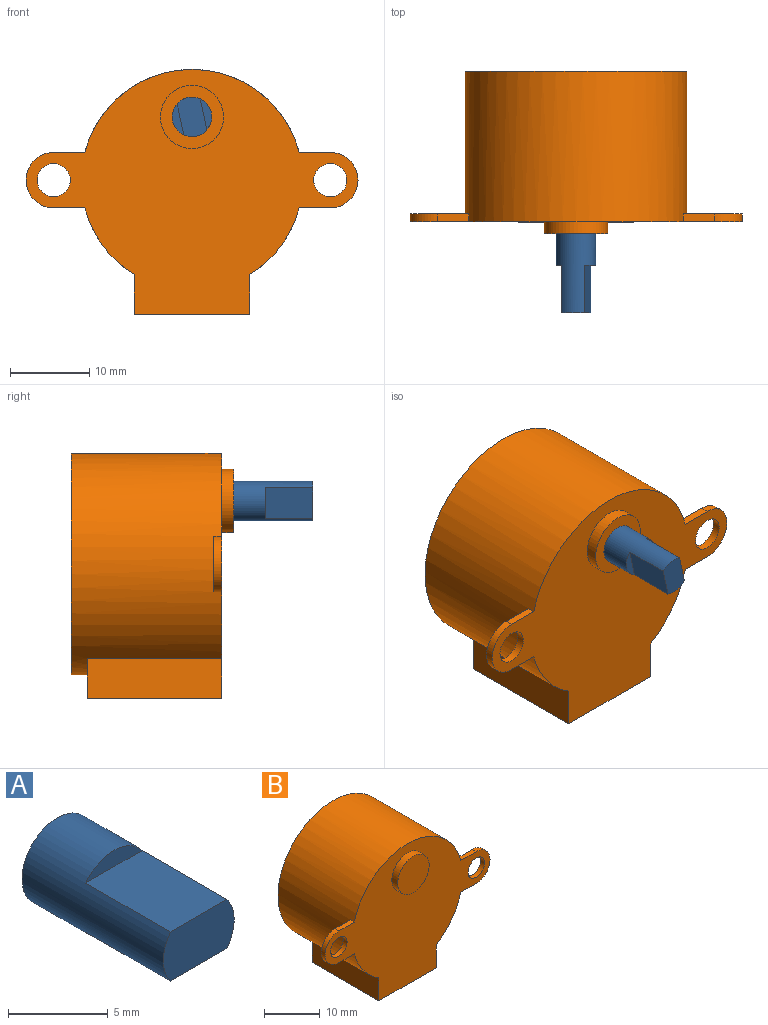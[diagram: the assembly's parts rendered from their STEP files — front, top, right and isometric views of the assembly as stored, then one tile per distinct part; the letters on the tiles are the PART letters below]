
ASSEMBLY  parts=2 mates=1
PART A: 7 faces, bbox 5x10x5 mm
  f0: plane 4x1mm, normal (0,-1,0), area 2.8mm2, adj f1,f4
  f1: cylinder r=2.5mm len=10mm, axis (0,1,0), area 101.4mm2, adj f0,f2,f3,f4,f5,f6
  f2: plane 4x1mm, normal (0,-1,0), area 2.8mm2, adj f1,f5
  f3: plane 5x5mm, normal (0,1,0), area 19.6mm2, adj f1
  f4: plane 6x4mm, normal (0,0,1), area 24mm2, adj f0,f1,f6
  f5: plane 6x4mm, normal (0,0,-1), area 24mm2, adj f1,f2,f6
  f6: plane 5x3mm, normal (0,-1,0), area 14mm2, adj f1,f4,f5
PART B: 19 faces, bbox 42x20.5x31 mm
  f0: cylinder r=14mm len=28mm, axis (0,-1,0), area 1396.1mm2, adj f1,f2,f3,f4,f7,f8,f11,f12
  f1: plane 28x28mm, normal (0,1,0), area 615.8mm2, adj f0
  f2: plane 42x31mm, normal (0,-1,0), area 680.8mm2, adj f0,f3,f4,f5,f6,f8,f9,f10
  f3: plane 3.94x1mm, normal (0,0,1), area 3.9mm2, adj f0,f2,f5,f7
  f4: plane 3.94x1mm, normal (0,0,-1), area 3.9mm2, adj f0,f2,f5,f7
  f5: cylinder r=3.5mm len=7mm, axis (0,-1,0), area 11mm2, adj f2,f3,f4,f7
  f6: cylinder r=2.1mm len=4.2mm, axis (0,-1,0), area 13.2mm2, adj f2,f7
  f7: plane 7.44x7mm, normal (0,1,0), area 30.9mm2, adj f0,f3,f4,f5,f6
  f8: plane 3.94x1mm, normal (0,0,1), area 3.9mm2, adj f0,f2,f9,f12
  f9: cylinder r=3.5mm len=7mm, axis (0,-1,0), area 11mm2, adj f2,f8,f11,f12
  f10: cylinder r=2.1mm len=4.2mm, axis (0,-1,0), area 13.2mm2, adj f2,f12
  f11: plane 3.94x1mm, normal (0,0,-1), area 3.9mm2, adj f0,f2,f9,f12
  f12: plane 7.44x7mm, normal (0,1,0), area 30.9mm2, adj f0,f8,f9,f10,f11
  f13: cylinder r=4mm len=8mm, axis (0,1,0), area 37.7mm2, adj f2,f14
  f14: plane 8x8mm, normal (0,-1,0), area 50.3mm2, adj f13
  f15: plane 17x5.05mm, normal (-1,0,0), area 85.9mm2, adj f0,f2,f16,f18
  f16: plane 17x14.6mm, normal (0,0,-1), area 248.2mm2, adj f2,f15,f17,f18
  f17: plane 17x5.05mm, normal (1,0,0), area 85.9mm2, adj f0,f2,f16,f18
  f18: plane 14.6x5.05mm, normal (0,1,0), area 53.5mm2, adj f0,f15,f16,f17
PLACE A rot(axis=(0,-1,0),101.9deg) t=(2.47,-3.68,11.02)mm
PLACE B t=(-5.35,-2.18,1.37)mm fixed
MATE revolute A.f1 <-> B.f13  axis (0,1,0) through (-5.35,-3.68,9.37)mm
